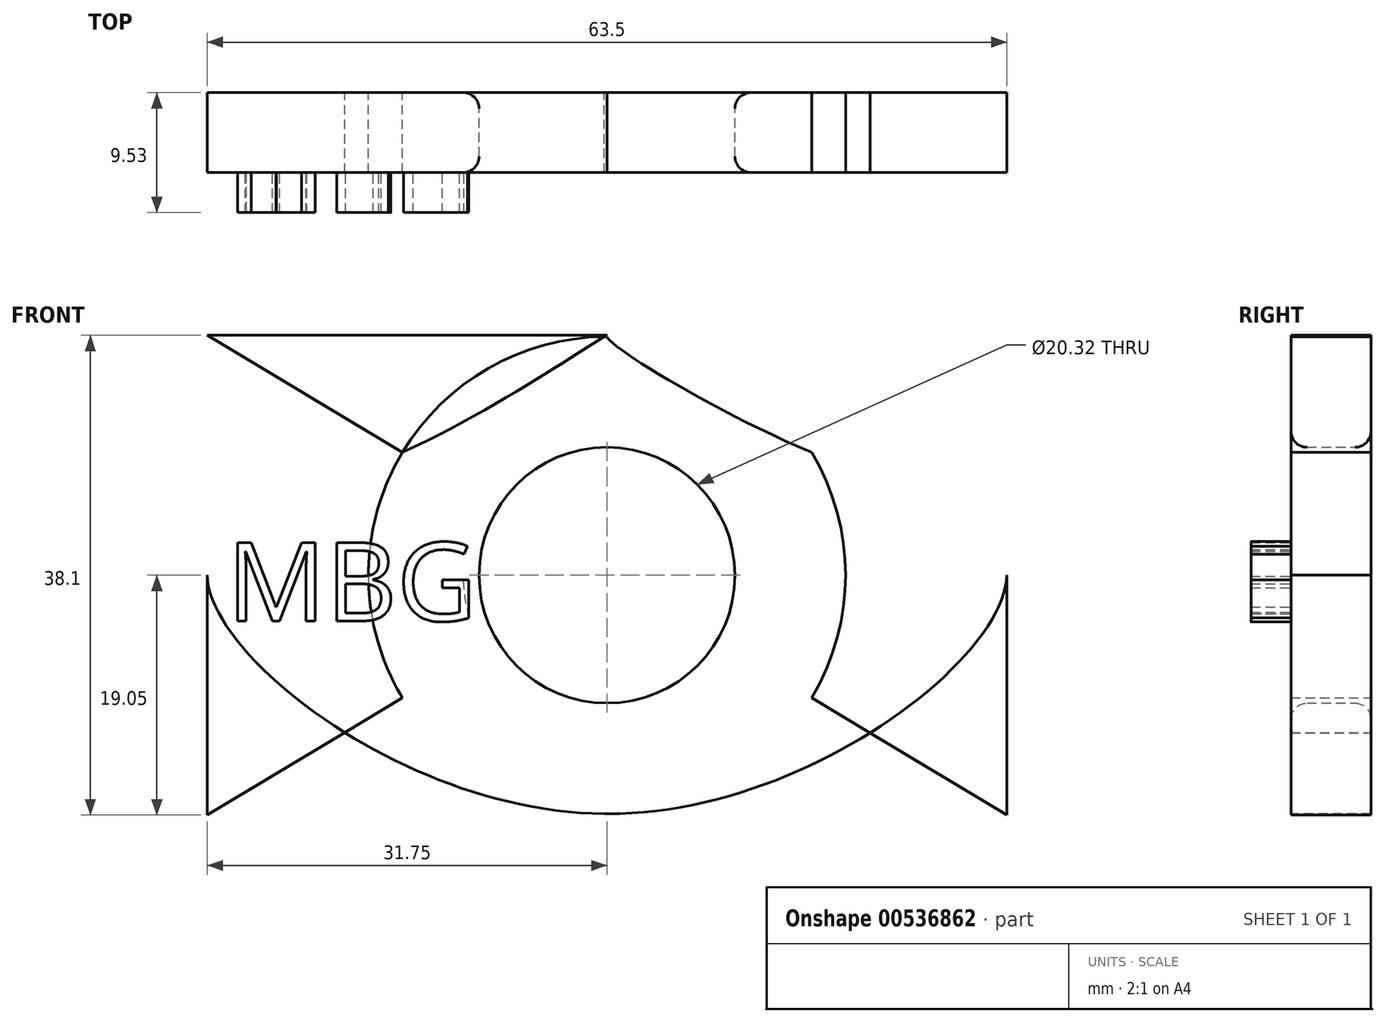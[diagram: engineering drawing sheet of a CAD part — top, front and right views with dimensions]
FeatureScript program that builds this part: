
annotation { "Feature Type Name" : "Feature", "Feature Type Description" : "" }
export const myFeature = defineFeature(function(context is Context, id is Id, definition is map)
    precondition{}
    {
        {
            var Q0;
            Q0=qCreatedBy(makeId("Front.planeOp"),FACE);
            var sketch = newSketch(context, id + "F0", { "sketchPlane" : qUnion([Q0])});
            skLineSegment(sketch, "E0.bottom", {"start": v(0, 0) * mm, "end": v(-63.5, 0) * mm});
            skLineSegment(sketch, "E0.top", {"start": v(0, -38.1) * mm, "end": v(-63.5, -38.1) * mm});
            skLineSegment(sketch, "E0.left", {"start": v(0, 0) * mm, "end": v(0, -38.1) * mm});
            skLineSegment(sketch, "E0.right", {"start": v(-63.5, 0) * mm, "end": v(-63.5, -38.1) * mm});
            skLineSegment(sketch, "E1", {"start": v(-63.5, 0) * mm, "end": v(0, -38.1) * mm});
            skLineSegment(sketch, "E2", {"start": v(0, 0) * mm, "end": v(-63.5, -38.1) * mm});
            skCircle(sketch, "E3", {"center": v(-31.75, -19.05) * mm, "radius": 10.16 * mm});
            skCircle(sketch, "E4", {"center": v(-31.75, -19.05) * mm, "radius": 18.95 * mm});
            skPoint(sketch, "E5.3.internal.snap0", {"position": v(-31.75, 0) * mm});
            skPoint(sketch, "E5.6.internal.snap0", {"position": v(-31.75, 0) * mm});
            skFitSpline(sketch, "E5", {"points": [v(-63.5, -19.05) * mm, v(-48, -9.3) * mm, v(-31.75, 0) * mm, v(-31.75, -0.1) * mm, v(-15.5, -9.3) * mm, v(0, -19.05) * mm, v(-31.75, -38) * mm, v(-63.5, -19.05) * mm]});
            skSolve(sketch);
        }
        {
            var Q0;
            {var subQ0=sQuery(id+"F0.wireOp",EDGE,"E5");var subQ1=sQuery(id+"F0.wireOp",EDGE,"E0.bottom");var subQ2=makeQuery(id+"F0.imprint","INTERSECT",VERTEX,{"disambiguationData":[OD(0.0)],"derivedFrom":[subQ1,subQ0]});Q0=makeQuery(id+"F0.imprint","IMPRINT",FACE,{"disambiguationData":[TD([[makeQuery(id+"F0.imprint","IMPRINT",EDGE,{"disambiguationData":[TD([[subQ2,-1.0]])],"derivedFrom":subQ1}),-1.0]])]});}
            var Q1;
            {var subQ0=sQuery(id+"F0.wireOp",EDGE,"E5");var subQ1=sQuery(id+"F0.wireOp",EDGE,"E0.left");var subQ2=makeQuery(id+"F0.imprint","INTERSECT",VERTEX,{"disambiguationData":[OD(0.0)],"derivedFrom":[subQ1,subQ0]});Q1=makeQuery(id+"F0.imprint","IMPRINT",FACE,{"disambiguationData":[TD([[makeQuery(id+"F0.imprint","IMPRINT",EDGE,{"disambiguationData":[TD([[subQ2,-1.0]])],"derivedFrom":subQ1}),1.0]])]});}
            var Q2;
            {var subQ0=sQuery(id+"F0.wireOp",EDGE,"E5");var subQ1=sQuery(id+"F0.wireOp",EDGE,"E0.right");var subQ2=makeQuery(id+"F0.imprint","INTERSECT",VERTEX,{"disambiguationData":[OD(0.0)],"derivedFrom":[subQ1,subQ0]});Q2=makeQuery(id+"F0.imprint","IMPRINT",FACE,{"disambiguationData":[TD([[makeQuery(id+"F0.imprint","IMPRINT",EDGE,{"disambiguationData":[TD([[subQ2,-1.0]])],"derivedFrom":subQ1}),-1.0]])]});}
            var Q3;
            {var subQ0=sQuery(id+"F0.wireOp",EDGE,"E5");var subQ1=sQuery(id+"F0.wireOp",EDGE,"E0.bottom");var subQ2=makeQuery(id+"F0.imprint","INTERSECT",VERTEX,{"disambiguationData":[OD(0.0)],"derivedFrom":[subQ1,subQ0]});Q3=makeQuery(id+"F0.imprint","IMPRINT",FACE,{"disambiguationData":[TD([[makeQuery(id+"F0.imprint","IMPRINT",EDGE,{"disambiguationData":[TD([[subQ2,-1.0]])],"derivedFrom":subQ1}),1.0]])]});}
            var Q4;
            {var subQ0=sQuery(id+"F0.wireOp",EDGE,"E5");var subQ1=sQuery(id+"F0.wireOp",EDGE,"E0.left");var subQ2=makeQuery(id+"F0.imprint","INTERSECT",VERTEX,{"disambiguationData":[OD(0.0)],"derivedFrom":[subQ1,subQ0]});Q4=makeQuery(id+"F0.imprint","IMPRINT",FACE,{"disambiguationData":[TD([[makeQuery(id+"F0.imprint","IMPRINT",EDGE,{"disambiguationData":[TD([[subQ2,-1.0]])],"derivedFrom":subQ1}),-1.0]])]});}
            var Q5;
            {var subQ0=sQuery(id+"F0.wireOp",EDGE,"E5");var subQ1=sQuery(id+"F0.wireOp",EDGE,"E0.right");var subQ2=makeQuery(id+"F0.imprint","INTERSECT",VERTEX,{"disambiguationData":[OD(0.0)],"derivedFrom":[subQ1,subQ0]});Q5=makeQuery(id+"F0.imprint","IMPRINT",FACE,{"disambiguationData":[TD([[makeQuery(id+"F0.imprint","IMPRINT",EDGE,{"disambiguationData":[TD([[subQ2,-1.0]])],"derivedFrom":subQ1}),1.0]])]});}
            var Q6;
            {var subQ4=sQuery(id+"F0.wireOp",EDGE,"E3");var subQ8=sQuery(id+"F0.wireOp",EDGE,"E1");var subQ9=makeQuery(id+"F0.imprint","INTERSECT",VERTEX,{"disambiguationData":[OD(0.0)],"derivedFrom":[subQ8,subQ4]});Q6=makeQuery(id+"F0.imprint","IMPRINT",FACE,{"disambiguationData":[TD([[makeQuery(id+"F0.imprint","IMPRINT",EDGE,{"disambiguationData":[TD([[subQ9,1.0]])],"derivedFrom":subQ4}),-1.0]])]});}
            var Q7;
            {var subQ0=sQuery(id+"F0.wireOp",EDGE,"E3");var subQ5=sQuery(id+"F0.wireOp",EDGE,"E2");var subQ6=makeQuery(id+"F0.imprint","INTERSECT",VERTEX,{"disambiguationData":[OD(1.0)],"derivedFrom":[subQ5,subQ0]});Q7=makeQuery(id+"F0.imprint","IMPRINT",FACE,{"disambiguationData":[TD([[makeQuery(id+"F0.imprint","IMPRINT",EDGE,{"disambiguationData":[TD([[subQ6,-1.0]])],"derivedFrom":subQ5}),-1.0]])]});}
            var Q8;
            {var subQ5=sQuery(id+"F0.wireOp",EDGE,"E3");var subQ7=sQuery(id+"F0.wireOp",EDGE,"E1");var subQ8=makeQuery(id+"F0.imprint","INTERSECT",VERTEX,{"disambiguationData":[OD(1.0)],"derivedFrom":[subQ7,subQ5]});Q8=makeQuery(id+"F0.imprint","IMPRINT",FACE,{"disambiguationData":[TD([[makeQuery(id+"F0.imprint","IMPRINT",EDGE,{"disambiguationData":[TD([[subQ8,-1.0]])],"derivedFrom":subQ7}),-1.0]])]});}
            var Q9;
            {var subQ0=sQuery(id+"F0.wireOp",EDGE,"E3");var subQ1=sQuery(id+"F0.wireOp",EDGE,"E1");var subQ2=makeQuery(id+"F0.imprint","INTERSECT",VERTEX,{"disambiguationData":[OD(1.0)],"derivedFrom":[subQ1,subQ0]});Q9=makeQuery(id+"F0.imprint","IMPRINT",FACE,{"disambiguationData":[TD([[makeQuery(id+"F0.imprint","IMPRINT",EDGE,{"disambiguationData":[TD([[subQ2,-1.0]])],"derivedFrom":subQ1}),1.0]])]});}
            var Q10;
            {var subQ0=sQuery(id+"F0.wireOp",EDGE,"E4");var subQ1=sQuery(id+"F0.wireOp",EDGE,"E1");var subQ2=makeQuery(id+"F0.imprint","INTERSECT",VERTEX,{"derivedFrom":[subQ1,subQ0]});Q10=makeQuery(id+"F0.imprint","IMPRINT",FACE,{"disambiguationData":[TD([[makeQuery(id+"F0.imprint","IMPRINT",EDGE,{"disambiguationData":[TD([[subQ2,-1.0]])],"derivedFrom":subQ1}),-1.0]])]});}
            var Q11;
            {var subQ0=sQuery(id+"F0.wireOp",EDGE,"E4");var subQ1=sQuery(id+"F0.wireOp",EDGE,"E2");var subQ2=makeQuery(id+"F0.imprint","INTERSECT",VERTEX,{"derivedFrom":[subQ1,subQ0]});Q11=makeQuery(id+"F0.imprint","IMPRINT",FACE,{"disambiguationData":[TD([[makeQuery(id+"F0.imprint","IMPRINT",EDGE,{"disambiguationData":[TD([[subQ2,-1.0]])],"derivedFrom":subQ1}),1.0]])]});}
            extrude(context, id + "F1", {"entities" : qUnion([Q0, Q1, Q2, Q3, Q4, Q5, Q6, Q7, Q8, Q9, Q10, Q11]), "depth" : 6.35 * mm, "offsetDistance" : 25.4 * mm});
        }
        {
            var Q0;
            Q0=makeQuery(id+"F1.opExtrude","CAP_EDGE",EDGE,{"disambiguationData":[OSD([sQuery(id+"F0.wireOp",EDGE,"E3")])],"isStart":false});
            var Q1;
            Q1=makeQuery(id+"F1.opExtrude","CAP_EDGE",EDGE,{"disambiguationData":[OSD([sQuery(id+"F0.wireOp",EDGE,"E3")])],"isStart":true});
            fillet(context, id + "F2", {"entities" : qUnion([Q0, Q1]), "radius" : 1.27 * mm, "tangentPropagation" : true, "allowEdgeOverflow" : false});
        }
        {
            var Q0;
            Q0=makeQuery(id+"F1.opExtrude","CAP_FACE",FACE,{"disambiguationData":[OSD([sQuery(id+"F0.wireOp",EDGE,"E3"),sQuery(id+"F0.wireOp",EDGE,"E5")])],"isStart":false});
            var sketch = newSketch(context, id + "F3", { "sketchPlane" : qUnion([Q0])});
            skText(sketch, "E6", { "text": "MBG", "fontName": "OpenSans-Regular.ttf"});
            const initialGuessF3  = {"E6": [-0.06194, -0.02268, 1, 0, 0.00627]};
            skSetInitialGuess(sketch, initialGuessF3);
            skSolve(sketch);
        }
        {
            var Q0;
            Q0 = qSketchRegion(id + "F3", true);
            extrude(context, id + "F4", {"entities" : qUnion([Q0]), "operationType" : NewBodyOperationType.ADD, "depth" : 3.17 * mm, "offsetDistance" : 25.4 * mm});
        }
    });
